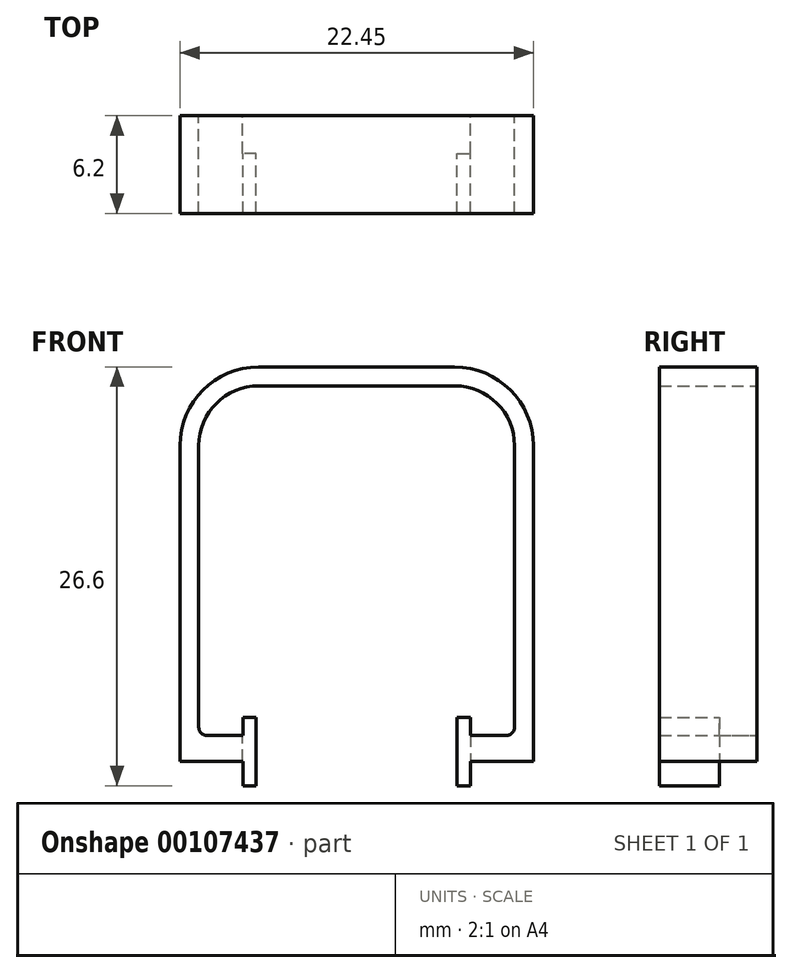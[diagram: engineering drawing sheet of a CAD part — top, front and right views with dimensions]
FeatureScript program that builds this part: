
annotation { "Feature Type Name" : "Feature", "Feature Type Description" : "" }
export const myFeature = defineFeature(function(context is Context, id is Id, definition is map)
    precondition{}
    {
        {
            var Q0;
            Q0=qCreatedBy(makeId("Front.planeOp"),FACE);
            var sketch = newSketch(context, id + "F0", { "sketchPlane" : qUnion([Q0])});
            skLineSegment(sketch, "E0.bottom", {"start": v(-46.55, 25.76) * mm, "end": v(33.45, 25.76) * mm});
            skLineSegment(sketch, "E0.top", {"start": v(-46.55, -24.24) * mm, "end": v(33.45, -24.24) * mm});
            skLineSegment(sketch, "E0.left", {"start": v(-51.55, 20.76) * mm, "end": v(-51.55, -19.24) * mm});
            skLineSegment(sketch, "E0.right", {"start": v(38.45, 20.76) * mm, "end": v(38.45, -19.24) * mm});
            skArc(sketch, "E1.filletArc", {"start": v(-46.55, 25.76) * mm, "mid": v(-50.09, 24.3) * mm, "end": v(-51.55, 20.76) * mm});
            skArc(sketch, "E2.filletArc", {"start": v(38.45, 20.76) * mm, "mid": v(36.98, 24.3) * mm, "end": v(33.45, 25.76) * mm});
            skArc(sketch, "E3.filletArc", {"start": v(33.45, -24.24) * mm, "mid": v(36.98, -22.77) * mm, "end": v(38.45, -19.24) * mm});
            skArc(sketch, "E4.filletArc", {"start": v(-51.55, -19.24) * mm, "mid": v(-50.09, -22.77) * mm, "end": v(-46.55, -24.24) * mm});
            skSolve(sketch);
        }
        {
            var Q0;
            Q0=makeQuery(id+"F0.imprint","IMPRINT",FACE,{"disambiguationData":[TD([[makeQuery(id+"F0.imprint","IMPRINT",EDGE,{"derivedFrom":sQuery(id+"F0.wireOp",EDGE,"E0.bottom")}),-1.0]])]});
            extrude(context, id + "F1", {"entities" : qUnion([Q0]), "depth" : 9.8 * mm});
        }
        {
            var Q0;
            Q0=makeQuery(id+"F1.opExtrude","CAP_FACE",FACE,{"disambiguationData":[OSD([sQuery(id+"F0.wireOp",EDGE,"E0.bottom"),sQuery(id+"F0.wireOp",EDGE,"E0.top"),sQuery(id+"F0.wireOp",EDGE,"E0.left"),sQuery(id+"F0.wireOp",EDGE,"E0.right"),sQuery(id+"F0.wireOp",EDGE,"E1.filletArc"),sQuery(id+"F0.wireOp",EDGE,"E2.filletArc"),sQuery(id+"F0.wireOp",EDGE,"E3.filletArc"),sQuery(id+"F0.wireOp",EDGE,"E4.filletArc")])],"isStart":false});
            shell(context, id + "F2", {"entities" : qUnion([Q0]), "thickness" : 2.5 * mm});
        }
        {
            var Q0;
            {var subQ0=sQuery(id+"F0.wireOp",EDGE,"E0.bottom");Q0=makeQuery(id+"F2.opShell","OFFSET_EDGE",EDGE,{"disambiguationData":[OSD([subQ0]),TDD([makeQuery(id+"F1.opExtrude","CAP_EDGE",EDGE,{"disambiguationData":[OSD([subQ0])],"isStart":true})])]});}
            fillet(context, id + "F3", {"entities" : qUnion([Q0]), "radius" : 5 * mm, "tangentPropagation" : true, "allowEdgeOverflow" : false});
        }
        {
            var Q0;
            {var subQ0=sQuery(id+"F0.wireOp",EDGE,"E0.bottom");Q0=makeQuery(id+"F2.opShell","OFFSET_EDGE",EDGE,{"disambiguationData":[OSD([subQ0]),TDD([makeQuery(id+"F1.opExtrude","CAP_EDGE",EDGE,{"disambiguationData":[OSD([subQ0])],"isStart":false})])]});}
            fillet(context, id + "F4", {"entities" : qUnion([Q0]), "radius" : 5 * mm, "tangentPropagation" : true, "allowEdgeOverflow" : false});
        }
        {
            var Q0;
            Q0=makeQuery(id+"F1.opExtrude","CAP_EDGE",EDGE,{"disambiguationData":[OSD([sQuery(id+"F0.wireOp",EDGE,"E0.bottom")])],"isStart":true});
            fillet(context, id + "F5", {"entities" : qUnion([Q0]), "radius" : 7 * mm, "tangentPropagation" : true, "allowEdgeOverflow" : false});
        }
        {
            var Q0;
            Q0=qCreatedBy(makeId("Front.planeOp"),FACE);
            var sketch = newSketch(context, id + "F6", { "sketchPlane" : qUnion([Q0])});
            skLineSegment(sketch, "E5", {"start": v(38.6, 0) * mm, "end": v(-51.4, 0) * mm, "construction": true});
            skPoint(sketch, "E6", {"position": v(-6.4, 0) * mm});
            skLineSegment(sketch, "E7", {"start": v(-6.4, -35.43) * mm, "end": v(-6.4, 48.54) * mm, "construction": true});
            skCircle(sketch, "E8", {"center": v(-6.4, 0) * mm, "radius": 4.5 * mm});
            skSolve(sketch);
        }
        {
            var Q0;
            Q0=makeQuery(id+"F6.imprint","IMPRINT",FACE,{"disambiguationData":[TD([[makeQuery(id+"F6.imprint","IMPRINT",EDGE,{"derivedFrom":sQuery(id+"F6.wireOp",EDGE,"E8")}),1.0]])]});
            var Q1;
            Q1=sQuery(id+"F6.wireOp",EDGE,"E8");
            extrude(context, id + "F7", {"entities" : qUnion([Q0]), "surfaceEntities" : qUnion([Q1]), "oppositeDirection" : true, "depth" : 130 * mm});
        }
        {
            var Q0;
            Q0=makeQuery(id+"F7.opExtrude","CAP_FACE",FACE,{"disambiguationData":[OSD([sQuery(id+"F6.wireOp",EDGE,"E8")])],"isStart":false});
            shell(context, id + "F8", {"entities" : qUnion([Q0]), "thickness" : 2.5 * mm});
        }
        {
            var Q0;
            Q0=makeQuery(id+"F7.opExtrude","SWEPT_BODY",BODY,{"disambiguationData":[OSD([sQuery(id+"F6.wireOp",EDGE,"E8")])]});
            deleteBodies(context, id + "F9", {"entities" : qUnion([Q0])});
        }
        {
            var Q0;
            Q0=makeQuery(id+"F1.opExtrude","SWEPT_BODY",BODY,{"disambiguationData":[OSD([sQuery(id+"F0.wireOp",EDGE,"E0.bottom"),sQuery(id+"F0.wireOp",EDGE,"E0.top"),sQuery(id+"F0.wireOp",EDGE,"E0.left"),sQuery(id+"F0.wireOp",EDGE,"E0.right"),sQuery(id+"F0.wireOp",EDGE,"E1.filletArc"),sQuery(id+"F0.wireOp",EDGE,"E2.filletArc"),sQuery(id+"F0.wireOp",EDGE,"E3.filletArc"),sQuery(id+"F0.wireOp",EDGE,"E4.filletArc")])]});
            deleteBodies(context, id + "F10", {"entities" : qUnion([Q0])});
        }
        {
            var Q0;
            Q0=qCreatedBy(makeId("Front.planeOp"),FACE);
            var sketch = newSketch(context, id + "F11", { "sketchPlane" : qUnion([Q0])});
            skLineSegment(sketch, "E9.bottom", {"start": v(-55.87, 46.45) * mm, "end": v(-43.42, 46.45) * mm});
            skLineSegment(sketch, "E9.left", {"start": v(-60.87, 41.45) * mm, "end": v(-60.87, 21.4) * mm});
            skLineSegment(sketch, "E9.right", {"start": v(-38.42, 41.45) * mm, "end": v(-38.42, 21.4) * mm});
            skPoint(sketch, "E10.visualSharp", {"position": v(-60.87, 46.45) * mm});
            skArc(sketch, "E10.filletArc", {"start": v(-55.87, 46.45) * mm, "mid": v(-59.4, 44.98) * mm, "end": v(-60.87, 41.45) * mm});
            skPoint(sketch, "E11.visualSharp", {"position": v(-38.42, 46.45) * mm});
            skArc(sketch, "E11.filletArc", {"start": v(-38.42, 41.45) * mm, "mid": v(-39.89, 44.98) * mm, "end": v(-43.42, 46.45) * mm});
            skLineSegment(sketch, "E12.0", {"start": v(-39.62, 41.45) * mm, "end": v(-39.62, 23.05) * mm});
            skLineSegment(sketch, "E12.1", {"start": v(-59.67, 41.45) * mm, "end": v(-59.67, 23.05) * mm});
            skArc(sketch, "E12.2", {"start": v(-55.87, 45.25) * mm, "mid": v(-58.56, 44.14) * mm, "end": v(-59.67, 41.45) * mm});
            skLineSegment(sketch, "E12.3", {"start": v(-55.87, 45.25) * mm, "end": v(-43.42, 45.25) * mm});
            skArc(sketch, "E12.4", {"start": v(-39.62, 41.45) * mm, "mid": v(-40.74, 44.14) * mm, "end": v(-43.42, 45.25) * mm});
            skLineSegment(sketch, "E13", {"start": v(-60.87, 21.4) * mm, "end": v(-56.87, 21.4) * mm});
            skLineSegment(sketch, "E14", {"start": v(-38.42, 21.4) * mm, "end": v(-42.42, 21.4) * mm});
            skLineSegment(sketch, "E15", {"start": v(-59.67, 23.05) * mm, "end": v(-56.87, 23.05) * mm});
            skLineSegment(sketch, "E16", {"start": v(-39.62, 23.05) * mm, "end": v(-42.42, 23.05) * mm});
            skLineSegment(sketch, "E17", {"start": v(-56.02, 24.2) * mm, "end": v(-56.02, 19.85) * mm});
            skLineSegment(sketch, "E18", {"start": v(-43.27, 24.2) * mm, "end": v(-43.27, 19.85) * mm});
            skLineSegment(sketch, "E19", {"start": v(-56.02, 24.2) * mm, "end": v(-56.87, 24.2) * mm});
            skLineSegment(sketch, "E20", {"start": v(-56.02, 19.85) * mm, "end": v(-56.87, 19.85) * mm});
            skLineSegment(sketch, "E21", {"start": v(-56.87, 19.85) * mm, "end": v(-56.87, 21.4) * mm});
            skLineSegment(sketch, "E22", {"start": v(-43.27, 24.2) * mm, "end": v(-42.42, 24.2) * mm});
            skLineSegment(sketch, "E23", {"start": v(-43.27, 19.85) * mm, "end": v(-42.42, 19.85) * mm});
            skLineSegment(sketch, "E24", {"start": v(-42.42, 19.85) * mm, "end": v(-42.42, 21.4) * mm});
            skPoint(sketch, "E25.orphan", {"position": v(-56.02, 23.05) * mm});
            skPoint(sketch, "E26.orphan", {"position": v(-56.02, 21.4) * mm});
            skLineSegment(sketch, "E27.trimOffspring", {"start": v(-56.87, 23.05) * mm, "end": v(-56.87, 24.2) * mm});
            skPoint(sketch, "E28.orphan", {"position": v(-59.67, 21.4) * mm});
            skPoint(sketch, "E29.orphan", {"position": v(-43.27, 23.05) * mm});
            skPoint(sketch, "E30.orphan", {"position": v(-43.27, 21.4) * mm});
            skLineSegment(sketch, "E31.trimOffspring", {"start": v(-42.42, 23.05) * mm, "end": v(-42.42, 24.2) * mm});
            skPoint(sketch, "E32.orphan", {"position": v(-39.62, 21.43) * mm});
            skSolve(sketch);
        }
        {
            var Q0;
            Q0=makeQuery(id+"F11.imprint","IMPRINT",FACE,{"disambiguationData":[TD([[makeQuery(id+"F11.imprint","IMPRINT",EDGE,{"derivedFrom":sQuery(id+"F11.wireOp",EDGE,"E9.bottom")}),-1.0]])]});
            var Q1;
            {var subQ0=sQuery(id+"F11.wireOp",EDGE,"E13");var subQ1=sQuery(id+"F11.wireOp",EDGE,"E9.left");var subQ2=makeQuery(id+"F11.imprint","INTERSECT",VERTEX,{"derivedFrom":[subQ1,subQ0]});Q1=makeQuery(id+"F11.imprint","IMPRINT",FACE,{"disambiguationData":[TD([[makeQuery(id+"F11.imprint","IMPRINT",EDGE,{"disambiguationData":[TD([[subQ2,1.0]])],"derivedFrom":subQ1}),1.0]])]});}
            var Q2;
            {var subQ0=sQuery(id+"F11.wireOp",EDGE,"E13");var subQ1=sQuery(id+"F11.wireOp",EDGE,"E12.1");var subQ2=makeQuery(id+"F11.imprint","INTERSECT",VERTEX,{"derivedFrom":[subQ1,subQ0]});Q2=makeQuery(id+"F11.imprint","IMPRINT",FACE,{"disambiguationData":[TD([[makeQuery(id+"F11.imprint","IMPRINT",EDGE,{"disambiguationData":[TD([[subQ2,1.0]])],"derivedFrom":subQ1}),1.0]])]});}
            var Q3;
            {var subQ0=sQuery(id+"F11.wireOp",EDGE,"E17");var subQ1=sQuery(id+"F11.wireOp",EDGE,"E13");var subQ2=makeQuery(id+"F11.imprint","INTERSECT",VERTEX,{"derivedFrom":[subQ1,subQ0]});Q3=makeQuery(id+"F11.imprint","IMPRINT",FACE,{"disambiguationData":[TD([[makeQuery(id+"F11.imprint","IMPRINT",EDGE,{"disambiguationData":[TD([[subQ2,1.0]])],"derivedFrom":subQ1}),1.0]])]});}
            var Q4;
            {var subQ5=sQuery(id+"F11.wireOp",EDGE,"E19");Q4=makeQuery(id+"F11.imprint","IMPRINT",FACE,{"disambiguationData":[TD([[makeQuery(id+"F11.imprint","IMPRINT",EDGE,{"derivedFrom":subQ5}),1.0]])]});}
            var Q5;
            {var subQ5=sQuery(id+"F11.wireOp",EDGE,"E20");Q5=makeQuery(id+"F11.imprint","IMPRINT",FACE,{"disambiguationData":[TD([[makeQuery(id+"F11.imprint","IMPRINT",EDGE,{"derivedFrom":subQ5}),-1.0]])]});}
            var Q6;
            {var subQ5=sQuery(id+"F11.wireOp",EDGE,"E22");Q6=makeQuery(id+"F11.imprint","IMPRINT",FACE,{"disambiguationData":[TD([[makeQuery(id+"F11.imprint","IMPRINT",EDGE,{"derivedFrom":subQ5}),-1.0]])]});}
            var Q7;
            {var subQ5=sQuery(id+"F11.wireOp",EDGE,"E23");Q7=makeQuery(id+"F11.imprint","IMPRINT",FACE,{"disambiguationData":[TD([[makeQuery(id+"F11.imprint","IMPRINT",EDGE,{"derivedFrom":subQ5}),1.0]])]});}
            var Q8;
            {var subQ0=sQuery(id+"F11.wireOp",EDGE,"E18");var subQ1=sQuery(id+"F11.wireOp",EDGE,"E14");var subQ2=makeQuery(id+"F11.imprint","INTERSECT",VERTEX,{"derivedFrom":[subQ1,subQ0]});Q8=makeQuery(id+"F11.imprint","IMPRINT",FACE,{"disambiguationData":[TD([[makeQuery(id+"F11.imprint","IMPRINT",EDGE,{"disambiguationData":[TD([[subQ2,1.0]])],"derivedFrom":subQ1}),-1.0]])]});}
            var Q9;
            {var subQ0=sQuery(id+"F11.wireOp",EDGE,"E14");var subQ1=sQuery(id+"F11.wireOp",EDGE,"E9.right");var subQ2=makeQuery(id+"F11.imprint","INTERSECT",VERTEX,{"derivedFrom":[subQ1,subQ0]});Q9=makeQuery(id+"F11.imprint","IMPRINT",FACE,{"disambiguationData":[TD([[makeQuery(id+"F11.imprint","IMPRINT",EDGE,{"disambiguationData":[TD([[subQ2,1.0]])],"derivedFrom":subQ1}),-1.0]])]});}
            extrude(context, id + "F12", {"entities" : qUnion([Q0, Q1, Q2, Q3, Q4, Q5, Q6, Q7, Q8, Q9]), "depth" : 6.2 * mm});
        }
        {
            var Q0;
            Q0=qCreatedBy(makeId("Front.planeOp"),FACE);
            var sketch = newSketch(context, id + "F13", { "sketchPlane" : qUnion([Q0])});
            skLineSegment(sketch, "E33.bottom", {"start": v(-56.88, 38.61) * mm, "end": v(-42.43, 38.61) * mm});
            skLineSegment(sketch, "E33.top", {"start": v(-56.88, 18.46) * mm, "end": v(-42.43, 18.46) * mm});
            skLineSegment(sketch, "E33.left", {"start": v(-56.88, 38.61) * mm, "end": v(-56.88, 18.46) * mm});
            skLineSegment(sketch, "E33.right", {"start": v(-42.43, 38.61) * mm, "end": v(-42.43, 18.46) * mm});
            skSolve(sketch);
        }
        {
            var Q0;
            Q0=makeQuery(id+"F13.imprint","IMPRINT",FACE,{"disambiguationData":[TD([[makeQuery(id+"F13.imprint","IMPRINT",EDGE,{"derivedFrom":sQuery(id+"F13.wireOp",EDGE,"E33.bottom")}),-1.0]])]});
            extrude(context, id + "F14", {"entities" : qUnion([Q0]), "operationType" : NewBodyOperationType.REMOVE, "depth" : 2.4 * mm});
        }
        {
            var Q0;
            Q0=makeQuery(id+"F12.opExtrude","SWEPT_EDGE",EDGE,{"disambiguationData":[OSD([sQuery(id+"F11.wireOp",EDGE,"E12.1"),sQuery(id+"F11.wireOp",EDGE,"E15")])]});
            fillet(context, id + "F15", {"entities" : qUnion([Q0]), "radius" : 0.5 * mm, "tangentPropagation" : true, "allowEdgeOverflow" : false});
        }
        {
            var Q0;
            Q0=makeQuery(id+"F12.opExtrude","SWEPT_EDGE",EDGE,{"disambiguationData":[OSD([sQuery(id+"F11.wireOp",EDGE,"E12.0"),sQuery(id+"F11.wireOp",EDGE,"E16")])]});
            fillet(context, id + "F16", {"entities" : qUnion([Q0]), "radius" : .5 * mm, "tangentPropagation" : true, "allowEdgeOverflow" : false});
        }
    });
